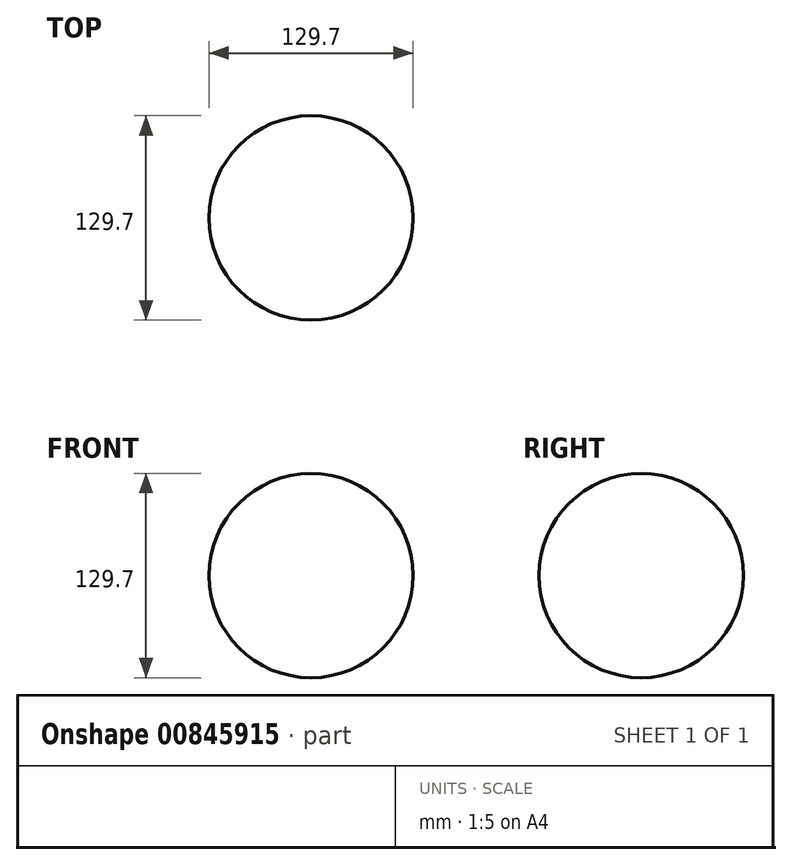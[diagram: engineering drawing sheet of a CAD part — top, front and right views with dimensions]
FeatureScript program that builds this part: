
annotation { "Feature Type Name" : "Feature", "Feature Type Description" : "" }
export const myFeature = defineFeature(function(context is Context, id is Id, definition is map)
    precondition{}
    {
        {
            var Q0;
            Q0=qCreatedBy(makeId("Front.planeOp"),FACE);
            var sketch = newSketch(context, id + "F0", { "sketchPlane" : qUnion([Q0])});
            skCircle(sketch, "E0", {"center": v(0, 0) * mm, "radius": 64.85 * mm});
            skLineSegment(sketch, "E1", {"start": v(0, 0) * mm, "end": v(0, 95.73) * mm});
            skLineSegment(sketch, "E2", {"start": v(0, 0) * mm, "end": v(0, -102.36) * mm});
            skSolve(sketch);
        }
        {
            var Q0;
            {var subQ0=sQuery(id+"F0.wireOp",EDGE,"E1");var subQ1=sQuery(id+"F0.wireOp",EDGE,"E0");var subQ2=makeQuery(id+"F0.imprint","INTERSECT",VERTEX,{"derivedFrom":[subQ1,subQ0]});Q0=makeQuery(id+"F0.imprint","IMPRINT",FACE,{"disambiguationData":[TD([[makeQuery(id+"F0.imprint","IMPRINT",EDGE,{"disambiguationData":[TD([[subQ2,1.0]])],"derivedFrom":subQ1}),1.0]])]});}
            var Q1;
            Q1=sQuery(id+"F0.wireOp",EDGE,"E2");
            revolve(context, id + "F1", {"surfaceOperationType" : NewSurfaceOperationType.NEW, "entities" : qUnion([Q0]), "axis" : qUnion([Q1]), "revolveType" : RevolveType.FULL});
        }
    });
